# Revit family: kawneer - 990 sliding door oxxo-25in_
name_source: partatom
category: Doors
revit_build: Autodesk Revit 2015 (Build: 20140905_0730(x64)
units: mm (PartAtom-declared; Revit-internal decimal feet)

## types (1)
- 990 Sliding Door OXXO
    2-Color Option = no
    Application = Low-rise, medium-rise, high-rise
    Assembly Code = B2030110
    CSI Masterformat Code = 08 32 13
    Color = any
    Configurations = OXXO
    Construction Type = Screw spline
    Depth = 0' - 4 1/2"
    Description = A slim sightline gives this sliding its uniques appearance.  For use in low, medium and high rise applications where large viewing area is desired.  The door is tested to several performance ratings and comes in a variety of configurations to suit any clients needs.
    Design Pressure = SGD-C30
SGD-HC40
SGD-HC60
    Door Corner Construction = Screw spline
    Door Panel Height = 6' - 10 1/2"
    Door Panel Material = Aluminum - ASTM B 221 - 6063-T6 alloy and temper
    Door Panel Width = 3' - 1"
    Frame Material = Aluminum - ASTM B 221 - 6063-T6 alloy and temper
    Function = Interior
    Function (Interior or Exterior) = Exterior
    Glass Capture = Captured
    Glass Installtion = Pre-glaze panels optional
    Glazing Thickness = 0' - 0"
    Height = 7' - 0"
    Hurricane Resistant Tested = product not tested
    Keywords = Entrance Door, Sliding Door, Condominium Door
    Manufacture Part Number = 990 Sliding Door
    Manufacturer = Kawneer
    Model = 990 Sliding Door
    Panel Inserts Material = Glass
    Product data url = https://bimobject.com
    Short Description = Non-Thermal Sliding Door
    Sightline = 0' - 6"
    Thermal transmittance = < 0.30 cfm/ft2  @ 6.24 psf (300 Pa)
    Type Comments = Non-Thermal Sliding Door
    Type of Glazing = Monolithic, Insulated glass
    URL = http://www.kawneer.com
    Wall Closure = By host
    Width = 12' - 0"

## geometry (parser evidence)
native form markers: Sweep x27
no freeform markers — native parametric forms only
